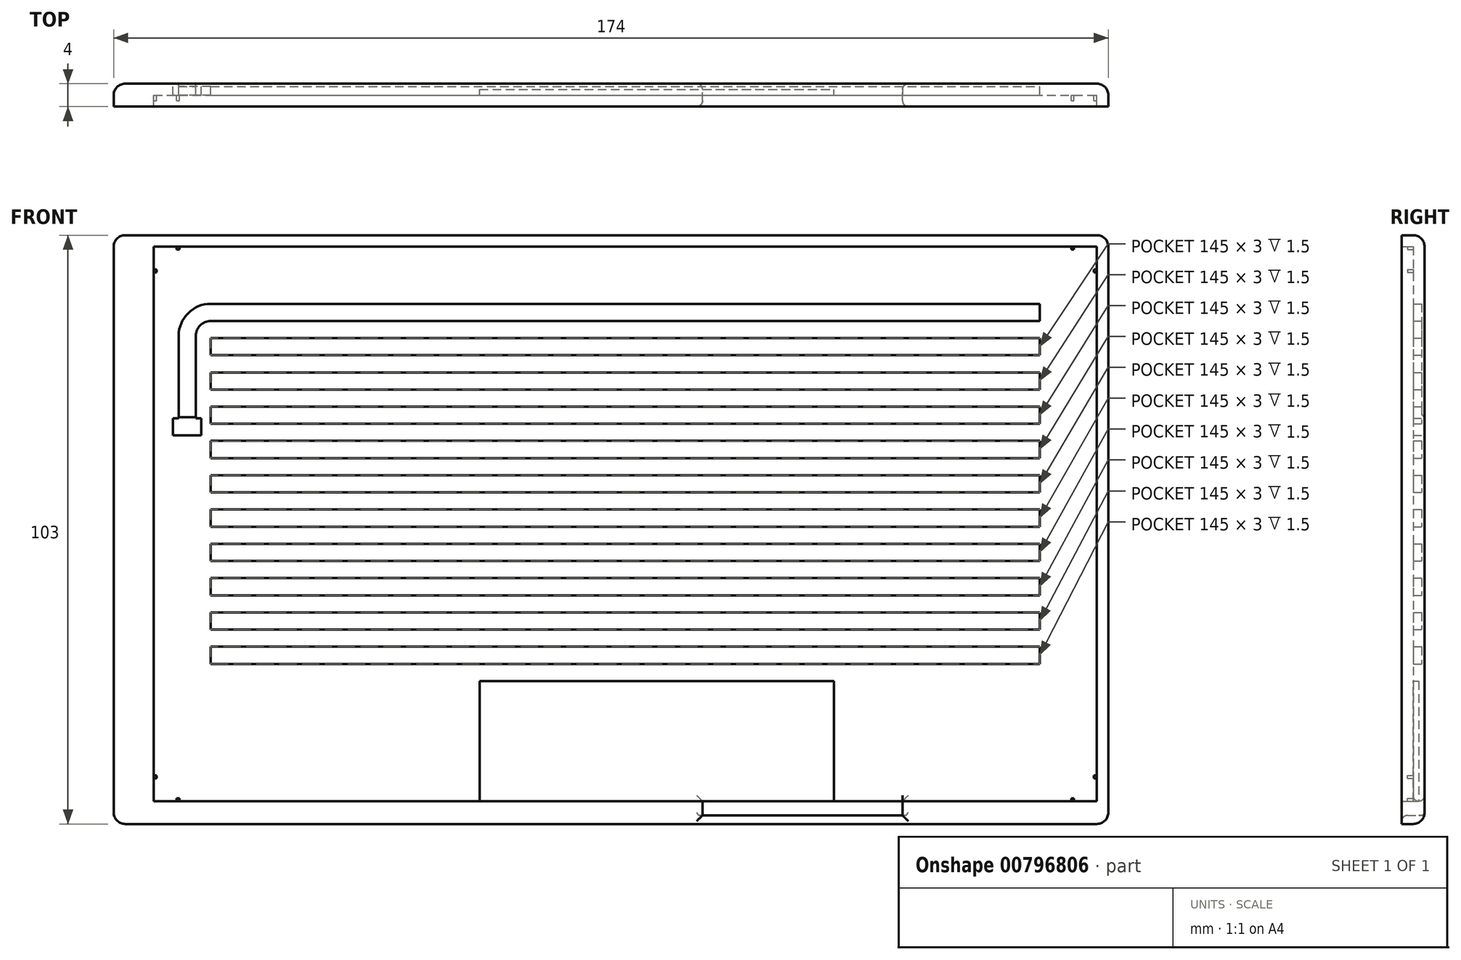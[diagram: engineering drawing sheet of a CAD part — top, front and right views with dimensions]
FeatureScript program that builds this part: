
annotation { "Feature Type Name" : "Feature", "Feature Type Description" : "" }
export const myFeature = defineFeature(function(context is Context, id is Id, definition is map)
    precondition{}
    {
        {
            var Q0;
            Q0=qCreatedBy(makeId("Front.planeOp"),FACE);
            var sketch = newSketch(context, id + "F0", { "sketchPlane" : qUnion([Q0])});
            skLineSegment(sketch, "E0.bottom", {"start": v(-82.5, 48.5) * mm, "end": v(82.5, 48.5) * mm});
            skLineSegment(sketch, "E0.top", {"start": v(-82.5, -48.5) * mm, "end": v(13.5, -48.5) * mm});
            skLineSegment(sketch, "E0.left", {"start": v(-82.5, 48.5) * mm, "end": v(-82.5, -48.5) * mm});
            skLineSegment(sketch, "E0.right", {"start": v(82.5, 48.5) * mm, "end": v(82.5, -48.5) * mm});
            skPoint(sketch, "E0.middle", {"position": v(0, 0) * mm});
            skLineSegment(sketch, "E1", {"start": v(-25.5, -48.5) * mm, "end": v(-25.5, -27.5) * mm});
            skLineSegment(sketch, "E2", {"start": v(-25.5, -27.5) * mm, "end": v(36.5, -27.5) * mm});
            skLineSegment(sketch, "E3", {"start": v(36.5, -27.5) * mm, "end": v(36.5, -48.5) * mm});
            skLineSegment(sketch, "E4", {"start": v(13.5, -48.5) * mm, "end": v(13.5, -48.5) * mm});
            skLineSegment(sketch, "E5", {"start": v(13.5, -48.5) * mm, "end": v(36.5, -48.5) * mm});
            skLineSegment(sketch, "E6", {"start": v(36.5, -48.5) * mm, "end": v(48.5, -48.5) * mm});
            skLineSegment(sketch, "E7", {"start": v(48.5, -48.5) * mm, "end": v(48.5, -48.5) * mm});
            skLineSegment(sketch, "E8.trimOffspring", {"start": v(48.5, -48.5) * mm, "end": v(82.5, -48.5) * mm});
            skLineSegment(sketch, "E9.bottom", {"start": v(-87.5, 50.5) * mm, "end": v(82.5, 50.5) * mm});
            skLineSegment(sketch, "E9.top", {"start": v(-87.5, -52.5) * mm, "end": v(82.5, -52.5) * mm});
            skLineSegment(sketch, "E9.left", {"start": v(-89.5, 48.5) * mm, "end": v(-89.5, -50.5) * mm});
            skLineSegment(sketch, "E9.right", {"start": v(84.5, 48.5) * mm, "end": v(84.5, -50.5) * mm});
            skLineSegment(sketch, "E10", {"start": v(13.5, -48.5) * mm, "end": v(13.5, -51) * mm});
            skLineSegment(sketch, "E11", {"start": v(13.5, -51) * mm, "end": v(48.5, -51) * mm});
            skLineSegment(sketch, "E12", {"start": v(48.5, -51) * mm, "end": v(48.5, -48.5) * mm});
            skArc(sketch, "E13", {"start": v(82.5, -52.5) * mm, "mid": v(83.91, -51.91) * mm, "end": v(84.5, -50.5) * mm});
            skArc(sketch, "E14", {"start": v(82.5, 50.5) * mm, "mid": v(83.91, 49.91) * mm, "end": v(84.5, 48.5) * mm});
            skArc(sketch, "E15", {"start": v(-89.5, 48.5) * mm, "mid": v(-88.91, 49.91) * mm, "end": v(-87.5, 50.5) * mm});
            skArc(sketch, "E16", {"start": v(-89.5, -50.5) * mm, "mid": v(-88.91, -51.91) * mm, "end": v(-87.5, -52.5) * mm});
            skLineSegment(sketch, "E17.bottom", {"start": v(-82.5, 44.5) * mm, "end": v(-82, 44.5) * mm});
            skLineSegment(sketch, "E17.top", {"start": v(-82.5, 44) * mm, "end": v(-82, 44) * mm});
            skLineSegment(sketch, "E17.left", {"start": v(-82.5, 44.5) * mm, "end": v(-82.5, 44) * mm});
            skLineSegment(sketch, "E17.right", {"start": v(-82, 44.5) * mm, "end": v(-82, 44) * mm});
            skLineSegment(sketch, "E18.bottom", {"start": v(-78.5, 48.5) * mm, "end": v(-78, 48.5) * mm});
            skLineSegment(sketch, "E18.top", {"start": v(-78.5, 48) * mm, "end": v(-78, 48) * mm});
            skLineSegment(sketch, "E18.left", {"start": v(-78.5, 48.5) * mm, "end": v(-78.5, 48) * mm});
            skLineSegment(sketch, "E18.right", {"start": v(-78, 48.5) * mm, "end": v(-78, 48) * mm});
            skLineSegment(sketch, "E19.bottom", {"start": v(-82, -44.5) * mm, "end": v(-82.5, -44.5) * mm});
            skLineSegment(sketch, "E19.top", {"start": v(-82, -44) * mm, "end": v(-82.5, -44) * mm});
            skLineSegment(sketch, "E19.left", {"start": v(-82, -44.5) * mm, "end": v(-82, -44) * mm});
            skLineSegment(sketch, "E19.right", {"start": v(-82.5, -44.5) * mm, "end": v(-82.5, -44) * mm});
            skLineSegment(sketch, "E20.bottom", {"start": v(-78, -48.5) * mm, "end": v(-78.5, -48.5) * mm});
            skLineSegment(sketch, "E20.top", {"start": v(-78, -48) * mm, "end": v(-78.5, -48) * mm});
            skLineSegment(sketch, "E20.left", {"start": v(-78, -48.5) * mm, "end": v(-78, -48) * mm});
            skLineSegment(sketch, "E20.right", {"start": v(-78.5, -48.5) * mm, "end": v(-78.5, -48) * mm});
            skLineSegment(sketch, "E21.bottom", {"start": v(78, 48.5) * mm, "end": v(78.5, 48.5) * mm});
            skLineSegment(sketch, "E21.top", {"start": v(78, 48) * mm, "end": v(78.5, 48) * mm});
            skLineSegment(sketch, "E21.left", {"start": v(78, 48.5) * mm, "end": v(78, 48) * mm});
            skLineSegment(sketch, "E21.right", {"start": v(78.5, 48.5) * mm, "end": v(78.5, 48) * mm});
            skLineSegment(sketch, "E22.bottom", {"start": v(82, 44.5) * mm, "end": v(82.5, 44.5) * mm});
            skLineSegment(sketch, "E22.top", {"start": v(82, 44) * mm, "end": v(82.5, 44) * mm});
            skLineSegment(sketch, "E22.left", {"start": v(82, 44.5) * mm, "end": v(82, 44) * mm});
            skLineSegment(sketch, "E22.right", {"start": v(82.5, 44.5) * mm, "end": v(82.5, 44) * mm});
            skLineSegment(sketch, "E23.bottom", {"start": v(82, -44) * mm, "end": v(82.5, -44) * mm});
            skLineSegment(sketch, "E23.top", {"start": v(82, -44.5) * mm, "end": v(82.5, -44.5) * mm});
            skLineSegment(sketch, "E23.left", {"start": v(82, -44) * mm, "end": v(82, -44.5) * mm});
            skLineSegment(sketch, "E23.right", {"start": v(82.5, -44) * mm, "end": v(82.5, -44.5) * mm});
            skLineSegment(sketch, "E24.bottom", {"start": v(78, -48) * mm, "end": v(78.5, -48) * mm});
            skLineSegment(sketch, "E24.top", {"start": v(78, -48.5) * mm, "end": v(78.5, -48.5) * mm});
            skLineSegment(sketch, "E24.left", {"start": v(78, -48) * mm, "end": v(78, -48.5) * mm});
            skLineSegment(sketch, "E24.right", {"start": v(78.5, -48) * mm, "end": v(78.5, -48.5) * mm});
            skLineSegment(sketch, "E25.bottom", {"start": v(-72.5, 38.5) * mm, "end": v(72.5, 38.5) * mm});
            skLineSegment(sketch, "E25.top", {"start": v(-72.5, 35.5) * mm, "end": v(72.5, 35.5) * mm});
            skLineSegment(sketch, "E25.left", {"start": v(-72.5, 38.5) * mm, "end": v(-72.5, 35.5) * mm});
            skLineSegment(sketch, "E25.right", {"start": v(72.5, 38.5) * mm, "end": v(72.5, 35.5) * mm});
            skLineSegment(sketch, "E26.0.1.0", {"start": v(-72.5, 32.5) * mm, "end": v(72.5, 32.5) * mm});
            skLineSegment(sketch, "E26.0.1.1", {"start": v(-72.5, 32.5) * mm, "end": v(-72.5, 29.5) * mm});
            skLineSegment(sketch, "E26.0.1.2", {"start": v(-72.5, 29.5) * mm, "end": v(72.5, 29.5) * mm});
            skLineSegment(sketch, "E26.0.1.3", {"start": v(72.5, 32.5) * mm, "end": v(72.5, 29.5) * mm});
            skLineSegment(sketch, "E26.0.2.0", {"start": v(-72.5, 26.5) * mm, "end": v(72.5, 26.5) * mm});
            skLineSegment(sketch, "E26.0.2.1", {"start": v(-72.5, 26.5) * mm, "end": v(-72.5, 23.5) * mm});
            skLineSegment(sketch, "E26.0.2.2", {"start": v(-72.5, 23.5) * mm, "end": v(72.5, 23.5) * mm});
            skLineSegment(sketch, "E26.0.2.3", {"start": v(72.5, 26.5) * mm, "end": v(72.5, 23.5) * mm});
            skLineSegment(sketch, "E26.0.3.0", {"start": v(-72.5, 20.5) * mm, "end": v(72.5, 20.5) * mm});
            skLineSegment(sketch, "E26.0.3.1", {"start": v(-72.5, 20.5) * mm, "end": v(-72.5, 17.5) * mm});
            skLineSegment(sketch, "E26.0.3.2", {"start": v(-72.5, 17.5) * mm, "end": v(72.5, 17.5) * mm});
            skLineSegment(sketch, "E26.0.3.3", {"start": v(72.5, 20.5) * mm, "end": v(72.5, 17.5) * mm});
            skLineSegment(sketch, "E26.0.4.0", {"start": v(-72.5, 14.5) * mm, "end": v(72.5, 14.5) * mm});
            skLineSegment(sketch, "E26.0.4.1", {"start": v(-72.5, 14.5) * mm, "end": v(-72.5, 11.5) * mm});
            skLineSegment(sketch, "E26.0.4.2", {"start": v(-72.5, 11.5) * mm, "end": v(72.5, 11.5) * mm});
            skLineSegment(sketch, "E26.0.4.3", {"start": v(72.5, 14.5) * mm, "end": v(72.5, 11.5) * mm});
            skLineSegment(sketch, "E26.0.5.0", {"start": v(-72.5, 8.5) * mm, "end": v(72.5, 8.5) * mm});
            skLineSegment(sketch, "E26.0.5.1", {"start": v(-72.5, 8.5) * mm, "end": v(-72.5, 5.5) * mm});
            skLineSegment(sketch, "E26.0.5.2", {"start": v(-72.5, 5.5) * mm, "end": v(72.5, 5.5) * mm});
            skLineSegment(sketch, "E26.0.5.3", {"start": v(72.5, 8.5) * mm, "end": v(72.5, 5.5) * mm});
            skLineSegment(sketch, "E26.0.6.0", {"start": v(-72.5, 2.5) * mm, "end": v(72.5, 2.5) * mm});
            skLineSegment(sketch, "E26.0.6.1", {"start": v(-72.5, 2.5) * mm, "end": v(-72.5, -0.5) * mm});
            skLineSegment(sketch, "E26.0.6.2", {"start": v(-72.5, -0.5) * mm, "end": v(72.5, -0.5) * mm});
            skLineSegment(sketch, "E26.0.6.3", {"start": v(72.5, 2.5) * mm, "end": v(72.5, -0.5) * mm});
            skLineSegment(sketch, "E26.0.7.0", {"start": v(-72.5, -3.5) * mm, "end": v(72.5, -3.5) * mm});
            skLineSegment(sketch, "E26.0.7.1", {"start": v(-72.5, -3.5) * mm, "end": v(-72.5, -6.5) * mm});
            skLineSegment(sketch, "E26.0.7.2", {"start": v(-72.5, -6.5) * mm, "end": v(72.5, -6.5) * mm});
            skLineSegment(sketch, "E26.0.7.3", {"start": v(72.5, -3.5) * mm, "end": v(72.5, -6.5) * mm});
            skLineSegment(sketch, "E26.direction1", {"start": v(-72.5, 38.5) * mm, "end": v(-72.5, 38.5) * mm});
            skLineSegment(sketch, "E26.direction2", {"start": v(-72.5, 38.5) * mm, "end": v(-72.5, 32.5) * mm, "construction": true});
            skLineSegment(sketch, "E27.0.0.8", {"start": v(-72.5, -9.5) * mm, "end": v(72.5, -9.5) * mm});
            skLineSegment(sketch, "E27.3.0.8", {"start": v(-72.5, -9.5) * mm, "end": v(-72.5, -12.5) * mm});
            skLineSegment(sketch, "E27.6.0.8", {"start": v(-72.5, -12.5) * mm, "end": v(72.5, -12.5) * mm});
            skLineSegment(sketch, "E27.9.0.8", {"start": v(72.5, -9.5) * mm, "end": v(72.5, -12.5) * mm});
            skLineSegment(sketch, "E27.0.0.9", {"start": v(-72.5, -15.5) * mm, "end": v(72.5, -15.5) * mm});
            skLineSegment(sketch, "E27.3.0.9", {"start": v(-72.5, -15.5) * mm, "end": v(-72.5, -18.5) * mm});
            skLineSegment(sketch, "E27.6.0.9", {"start": v(-72.5, -18.5) * mm, "end": v(72.5, -18.5) * mm});
            skLineSegment(sketch, "E27.9.0.9", {"start": v(72.5, -15.5) * mm, "end": v(72.5, -18.5) * mm});
            skLineSegment(sketch, "E27.0.0.10", {"start": v(-72.5, -21.5) * mm, "end": v(72.5, -21.5) * mm});
            skLineSegment(sketch, "E27.3.0.10", {"start": v(-72.5, -21.5) * mm, "end": v(-72.5, -24.5) * mm});
            skLineSegment(sketch, "E27.6.0.10", {"start": v(-72.5, -24.5) * mm, "end": v(72.5, -24.5) * mm});
            skLineSegment(sketch, "E27.9.0.10", {"start": v(72.5, -21.5) * mm, "end": v(72.5, -24.5) * mm});
            skLineSegment(sketch, "E28", {"start": v(-74.2, 15.5) * mm, "end": v(-79.1, 15.5) * mm});
            skLineSegment(sketch, "E29", {"start": v(-79.1, 15.5) * mm, "end": v(-79.1, 18.5) * mm});
            skLineSegment(sketch, "E30", {"start": v(-79.1, 18.5) * mm, "end": v(-74.2, 18.5) * mm});
            skLineSegment(sketch, "E31", {"start": v(-74.2, 18.5) * mm, "end": v(-74.2, 15.5) * mm});
            skArc(sketch, "E32", {"start": v(-72.5, 35.5) * mm, "mid": v(-74.37, 34.73) * mm, "end": v(-75.14, 32.86) * mm});
            skLineSegment(sketch, "E33", {"start": v(-75.14, 32.86) * mm, "end": v(-75.14, 18.5) * mm});
            skLineSegment(sketch, "E34.0", {"start": v(-78.14, 32.86) * mm, "end": v(-78.14, 18.5) * mm});
            skArc(sketch, "E34.1", {"start": v(-72.5, 38.5) * mm, "mid": v(-76.49, 36.85) * mm, "end": v(-78.14, 32.86) * mm});
            skSolve(sketch);
        }
        {
            var Q0;
            {var subQ0=sQuery(id+"F0.wireOp",EDGE,"E1");Q0=makeQuery(id+"F0.imprint","IMPRINT",FACE,{"disambiguationData":[TD([[makeQuery(id+"F0.imprint","IMPRINT",EDGE,{"derivedFrom":subQ0}),-1.0]])]});}
            extrude(context, id + "F1", {"entities" : qUnion([Q0]), "depth" : 1 * mm, "offsetDistance" : 25 * mm});
        }
        {
            var Q0;
            {var subQ26=sQuery(id+"F0.wireOp",EDGE,"E1");Q0=makeQuery(id+"F0.imprint","IMPRINT",FACE,{"disambiguationData":[TD([[makeQuery(id+"F0.imprint","IMPRINT",EDGE,{"derivedFrom":subQ26}),1.0]])]});}
            extrude(context, id + "F2", {"entities" : qUnion([Q0]), "operationType" : NewBodyOperationType.ADD, "depth" : 2 * mm, "offsetDistance" : 25 * mm});
        }
        {
            var Q0;
            Q0=makeQuery(id+"F0.imprint","IMPRINT",FACE,{"disambiguationData":[TD([[makeQuery(id+"F0.imprint","IMPRINT",EDGE,{"derivedFrom":sQuery(id+"F0.wireOp",EDGE,"E25.bottom")}),-1.0]])]});
            var Q1;
            Q1=makeQuery(id+"F0.imprint","IMPRINT",FACE,{"disambiguationData":[TD([[makeQuery(id+"F0.imprint","IMPRINT",EDGE,{"derivedFrom":sQuery(id+"F0.wireOp",EDGE,"E26.0.1.0")}),-1.0]])]});
            var Q2;
            Q2=makeQuery(id+"F0.imprint","IMPRINT",FACE,{"disambiguationData":[TD([[makeQuery(id+"F0.imprint","IMPRINT",EDGE,{"derivedFrom":sQuery(id+"F0.wireOp",EDGE,"E26.0.2.0")}),-1.0]])]});
            var Q3;
            Q3=makeQuery(id+"F0.imprint","IMPRINT",FACE,{"disambiguationData":[TD([[makeQuery(id+"F0.imprint","IMPRINT",EDGE,{"derivedFrom":sQuery(id+"F0.wireOp",EDGE,"E26.0.3.0")}),-1.0]])]});
            var Q4;
            Q4=makeQuery(id+"F0.imprint","IMPRINT",FACE,{"disambiguationData":[TD([[makeQuery(id+"F0.imprint","IMPRINT",EDGE,{"derivedFrom":sQuery(id+"F0.wireOp",EDGE,"E26.0.4.0")}),-1.0]])]});
            var Q5;
            Q5=makeQuery(id+"F0.imprint","IMPRINT",FACE,{"disambiguationData":[TD([[makeQuery(id+"F0.imprint","IMPRINT",EDGE,{"derivedFrom":sQuery(id+"F0.wireOp",EDGE,"E26.0.5.0")}),-1.0]])]});
            var Q6;
            Q6=makeQuery(id+"F0.imprint","IMPRINT",FACE,{"disambiguationData":[TD([[makeQuery(id+"F0.imprint","IMPRINT",EDGE,{"derivedFrom":sQuery(id+"F0.wireOp",EDGE,"E26.0.6.0")}),-1.0]])]});
            var Q7;
            Q7=makeQuery(id+"F0.imprint","IMPRINT",FACE,{"disambiguationData":[TD([[makeQuery(id+"F0.imprint","IMPRINT",EDGE,{"derivedFrom":sQuery(id+"F0.wireOp",EDGE,"E26.0.7.0")}),-1.0]])]});
            var Q8;
            Q8=makeQuery(id+"F0.imprint","IMPRINT",FACE,{"disambiguationData":[TD([[makeQuery(id+"F0.imprint","IMPRINT",EDGE,{"derivedFrom":sQuery(id+"F0.wireOp",EDGE,"E26.0.8.0")}),-1.0]])]});
            var Q9;
            Q9=makeQuery(id+"F0.imprint","IMPRINT",FACE,{"disambiguationData":[TD([[makeQuery(id+"F0.imprint","IMPRINT",EDGE,{"derivedFrom":sQuery(id+"F0.wireOp",EDGE,"E26.0.9.0")}),-1.0]])]});
            var Q10;
            Q10=makeQuery(id+"F0.imprint","IMPRINT",FACE,{"disambiguationData":[TD([[makeQuery(id+"F0.imprint","IMPRINT",EDGE,{"derivedFrom":sQuery(id+"F0.wireOp",EDGE,"E27.0.0.8")}),-1.0]])]});
            var Q11;
            Q11=makeQuery(id+"F0.imprint","IMPRINT",FACE,{"disambiguationData":[TD([[makeQuery(id+"F0.imprint","IMPRINT",EDGE,{"derivedFrom":sQuery(id+"F0.wireOp",EDGE,"E27.0.0.9")}),-1.0]])]});
            var Q12;
            Q12=makeQuery(id+"F0.imprint","IMPRINT",FACE,{"disambiguationData":[TD([[makeQuery(id+"F0.imprint","IMPRINT",EDGE,{"derivedFrom":sQuery(id+"F0.wireOp",EDGE,"E27.0.0.10")}),-1.0]])]});
            var Q13;
            Q13=makeQuery(id+"F0.imprint","IMPRINT",FACE,{"disambiguationData":[TD([[makeQuery(id+"F0.imprint","IMPRINT",EDGE,{"derivedFrom":sQuery(id+"F0.wireOp",EDGE,"E25.left")}),-1.0]])]});
            extrude(context, id + "F3", {"entities" : qUnion([Q0, Q1, Q2, Q3, Q4, Q5, Q6, Q7, Q8, Q9, Q10, Q11, Q12, Q13]), "operationType" : NewBodyOperationType.ADD, "depth" : 0.5 * mm, "offsetDistance" : 25 * mm});
        }
        {
            var Q0;
            {var subQ2=sQuery(id+"F0.wireOp",EDGE,"E17.bottom");Q0=makeQuery(id+"F0.imprint","IMPRINT",FACE,{"disambiguationData":[TD([[makeQuery(id+"F0.imprint","IMPRINT",EDGE,{"derivedFrom":subQ2}),-1.0]])]});}
            var Q1;
            Q1=makeQuery(id+"F0.imprint","IMPRINT",FACE,{"disambiguationData":[TD([[makeQuery(id+"F0.imprint","IMPRINT",EDGE,{"derivedFrom":sQuery(id+"F0.wireOp",EDGE,"E18.top")}),1.0]])]});
            var Q2;
            {var subQ0=sQuery(id+"F0.wireOp",EDGE,"E19.bottom");Q2=makeQuery(id+"F0.imprint","IMPRINT",FACE,{"disambiguationData":[TD([[makeQuery(id+"F0.imprint","IMPRINT",EDGE,{"derivedFrom":subQ0}),-1.0]])]});}
            var Q3;
            Q3=makeQuery(id+"F0.imprint","IMPRINT",FACE,{"disambiguationData":[TD([[makeQuery(id+"F0.imprint","IMPRINT",EDGE,{"derivedFrom":sQuery(id+"F0.wireOp",EDGE,"E20.top")}),1.0]])]});
            var Q4;
            {var subQ2=sQuery(id+"F0.wireOp",EDGE,"E23.bottom");Q4=makeQuery(id+"F0.imprint","IMPRINT",FACE,{"disambiguationData":[TD([[makeQuery(id+"F0.imprint","IMPRINT",EDGE,{"derivedFrom":subQ2}),-1.0]])]});}
            var Q5;
            Q5=makeQuery(id+"F0.imprint","IMPRINT",FACE,{"disambiguationData":[TD([[makeQuery(id+"F0.imprint","IMPRINT",EDGE,{"derivedFrom":sQuery(id+"F0.wireOp",EDGE,"E24.bottom")}),-1.0]])]});
            var Q6;
            Q6=makeQuery(id+"F0.imprint","IMPRINT",FACE,{"disambiguationData":[TD([[makeQuery(id+"F0.imprint","IMPRINT",EDGE,{"derivedFrom":sQuery(id+"F0.wireOp",EDGE,"E21.top")}),1.0]])]});
            var Q7;
            {var subQ2=sQuery(id+"F0.wireOp",EDGE,"E22.bottom");Q7=makeQuery(id+"F0.imprint","IMPRINT",FACE,{"disambiguationData":[TD([[makeQuery(id+"F0.imprint","IMPRINT",EDGE,{"derivedFrom":subQ2}),-1.0]])]});}
            extrude(context, id + "F4", {"entities" : qUnion([Q0, Q1, Q2, Q3, Q4, Q5, Q6, Q7]), "operationType" : NewBodyOperationType.ADD, "depth" : 3 * mm, "offsetDistance" : 25 * mm});
        }
        {
            var Q0;
            Q0=makeQuery(id+"F0.imprint","IMPRINT",FACE,{"disambiguationData":[TD([[makeQuery(id+"F0.imprint","IMPRINT",EDGE,{"derivedFrom":sQuery(id+"F0.wireOp",EDGE,"E9.bottom")}),-1.0]])]});
            extrude(context, id + "F5", {"entities" : qUnion([Q0]), "operationType" : NewBodyOperationType.ADD, "depth" : 4 * mm, "offsetDistance" : 25 * mm});
        }
        {
            var Q0;
            Q0=makeQuery(id+"F5.opExtrude","CAP_EDGE",EDGE,{"disambiguationData":[OSD([sQuery(id+"F0.wireOp",EDGE,"E9.right")])],"isStart":true});
            var Q1;
            Q1=makeQuery(id+"F5.opExtrude","CAP_EDGE",EDGE,{"disambiguationData":[OSD([sQuery(id+"F0.wireOp",EDGE,"E9.left")])],"isStart":true});
            var Q2;
            Q2=makeQuery(id+"F5.opExtrude","CAP_EDGE",EDGE,{"disambiguationData":[OSD([sQuery(id+"F0.wireOp",EDGE,"E9.bottom")])],"isStart":true});
            var Q3;
            Q3=makeQuery(id+"F5.opExtrude","CAP_EDGE",EDGE,{"disambiguationData":[OSD([sQuery(id+"F0.wireOp",EDGE,"E9.top")])],"isStart":true});
            fillet(context, id + "F6", {"entities" : qUnion([Q0, Q1, Q2, Q3]), "radius" : 2 * mm, "tangentPropagation" : true, "allowEdgeOverflow" : false});
        }
        {
            var Q0;
            Q0=makeQuery(id+"F5.opExtrude","CAP_EDGE",EDGE,{"disambiguationData":[OSD([sQuery(id+"F0.wireOp",EDGE,"E11")])],"isStart":false});
            var Q1;
            Q1=makeQuery(id+"F5.opExtrude","CAP_EDGE",EDGE,{"disambiguationData":[OSD([sQuery(id+"F0.wireOp",EDGE,"E12")])],"isStart":false});
            var Q2;
            Q2=makeQuery(id+"F5.opExtrude","CAP_EDGE",EDGE,{"disambiguationData":[OSD([sQuery(id+"F0.wireOp",EDGE,"E10")])],"isStart":false});
            var Q3;
            {var subQ3=sQuery(id+"F0.wireOp",EDGE,"E8.trimOffspring");var subQ4=sQuery(id+"F0.wireOp",EDGE,"E6");Q3=makeQuery(id+"F5.boolean.opBoolean","SPLIT",EDGE,{"disambiguationData":[topologyDisambiguationEdgeConnected([makeQuery(id+"F2.opExtrude","SWEPT_FACE",FACE,{"disambiguationData":[OSD([subQ3])]})])],"derivedFrom":makeQuery(id+"F2.opExtrude","CAP_EDGE",EDGE,{"disambiguationData":[OSD([subQ4,subQ3])],"isStart":false})});}
            var Q4;
            {var subQ0=sQuery(id+"F0.wireOp",EDGE,"E8.trimOffspring");var subQ1=sQuery(id+"F0.wireOp",EDGE,"E0.top");Q4=makeQuery(id+"F4.boolean.opBoolean","MERGE",EDGE,{"derivedFrom":[makeQuery(id+"F2.opExtrude","CAP_EDGE",EDGE,{"disambiguationData":[OSD([subQ1]),TDD([makeQuery(id+"F0.imprint","IMPRINT",EDGE,{"disambiguationData":[TD([[makeQuery(id+"F0.imprint","INTERSECT",VERTEX,{"derivedFrom":[subQ1,sQuery(id+"F0.wireOp",EDGE,"E20.right")]}),1.0]])],"derivedFrom":subQ1})])],"isStart":true}),makeQuery(id+"F2.opExtrude","CAP_EDGE",EDGE,{"disambiguationData":[OSD([subQ0])],"isStart":true}),makeQuery(id+"F2.boolean.opBoolean","MERGE",EDGE,{"derivedFrom":[makeQuery(id+"F1.opExtrude","CAP_EDGE",EDGE,{"disambiguationData":[OSD([subQ1,sQuery(id+"F0.wireOp",EDGE,"E5")])],"isStart":true}),makeQuery(id+"F2.opExtrude","CAP_EDGE",EDGE,{"disambiguationData":[OSD([subQ1]),TDD([makeQuery(id+"F0.imprint","IMPRINT",EDGE,{"disambiguationData":[TD([[makeQuery(id+"F0.imprint","INTERSECT",VERTEX,{"derivedFrom":[subQ1,sQuery(id+"F0.wireOp",EDGE,"E20.left")]}),-1.0]])],"derivedFrom":subQ1})])],"isStart":true}),makeQuery(id+"F2.opExtrude","CAP_EDGE",EDGE,{"disambiguationData":[OSD([sQuery(id+"F0.wireOp",EDGE,"E6"),subQ0])],"isStart":true})]}),makeQuery(id+"F4.opExtrude","CAP_EDGE",EDGE,{"disambiguationData":[OSD([subQ1])],"isStart":true}),makeQuery(id+"F4.opExtrude","CAP_EDGE",EDGE,{"disambiguationData":[OSD([subQ0])],"isStart":true})]});}
            var Q5;
            Q5=makeQuery(id+"F5.opExtrude","CAP_EDGE",EDGE,{"disambiguationData":[OSD([sQuery(id+"F0.wireOp",EDGE,"E10")])],"isStart":true});
            var Q6;
            Q6=makeQuery(id+"F5.opExtrude","CAP_EDGE",EDGE,{"disambiguationData":[OSD([sQuery(id+"F0.wireOp",EDGE,"E12")])],"isStart":true});
            fillet(context, id + "F7", {"entities" : qUnion([Q0, Q1, Q2, Q3, Q4, Q5, Q6]), "radius" : 1 * mm, "allowEdgeOverflow" : false});
        }
        {
            var Q0;
            Q0=makeQuery(id+"F3.opExtrude","CAP_EDGE",EDGE,{"disambiguationData":[OSD([sQuery(id+"F0.wireOp",EDGE,"E30")])],"isStart":false});
            fillet(context, id + "F8", {"entities" : qUnion([Q0]), "radius" : 1 * mm, "tangentPropagation" : true, "allowEdgeOverflow" : false});
        }
    });
